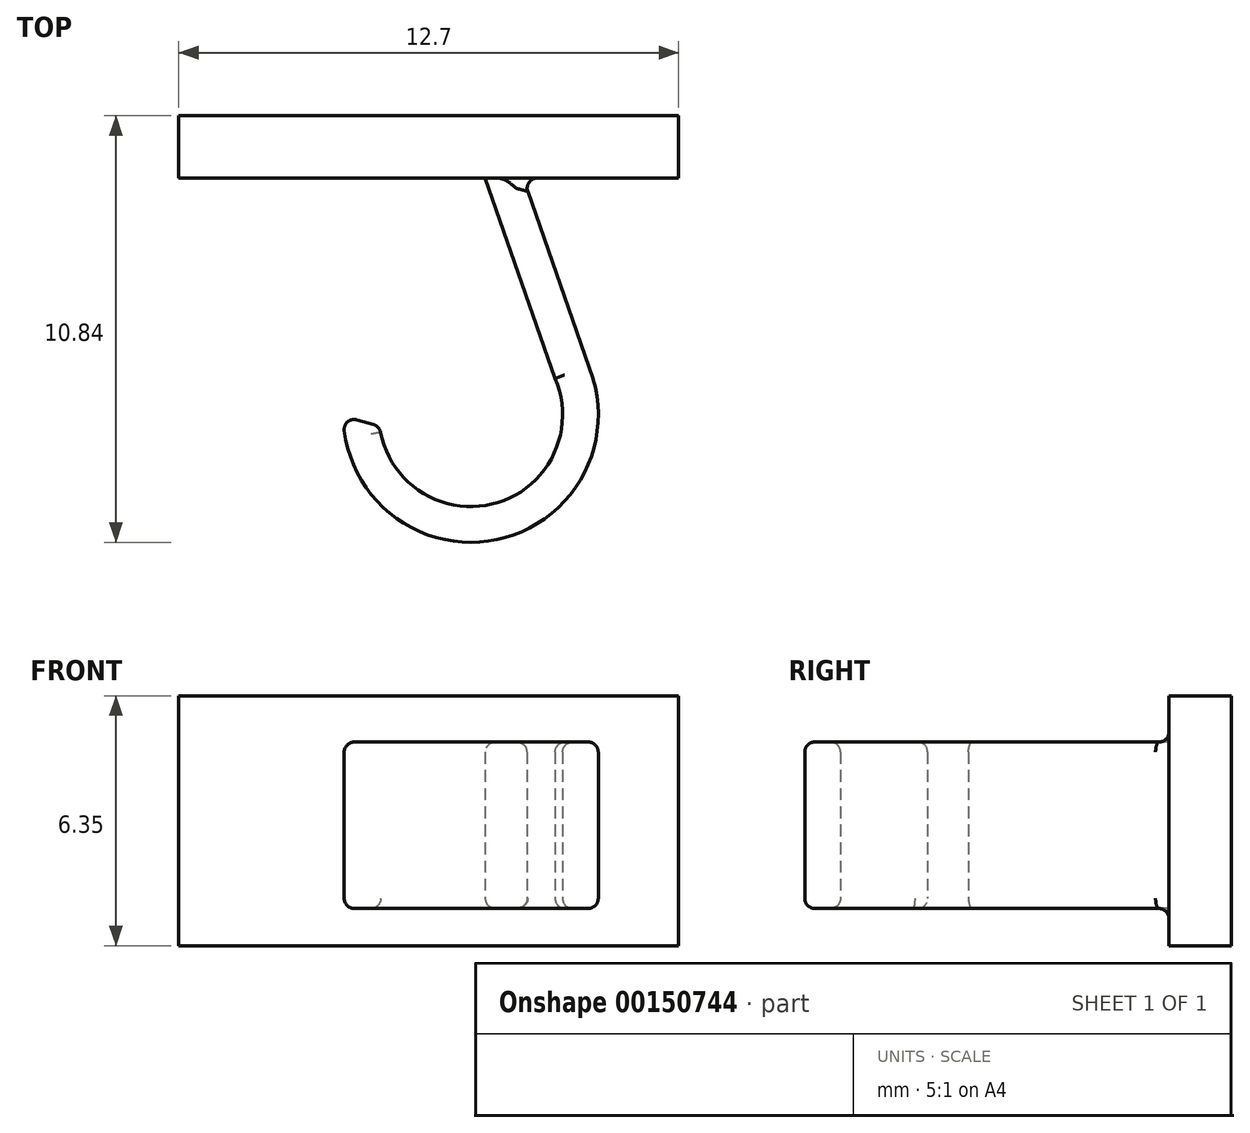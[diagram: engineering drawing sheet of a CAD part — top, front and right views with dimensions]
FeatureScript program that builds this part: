
annotation { "Feature Type Name" : "Feature", "Feature Type Description" : "" }
export const myFeature = defineFeature(function(context is Context, id is Id, definition is map)
    precondition{}
    {
        {
            var Q0;
            Q0=qCreatedBy(makeId("Front.planeOp"),FACE);
            var sketch = newSketch(context, id + "F0", { "sketchPlane" : qUnion([Q0])});
            skLineSegment(sketch, "E0.bottom", {"start": v(0, 0) * mm, "end": v(12.7, 0) * mm});
            skLineSegment(sketch, "E0.top", {"start": v(0, 6.35) * mm, "end": v(12.7, 6.35) * mm});
            skLineSegment(sketch, "E0.left", {"start": v(0, 0) * mm, "end": v(0, 6.35) * mm});
            skLineSegment(sketch, "E0.right", {"start": v(12.7, 0) * mm, "end": v(12.7, 6.35) * mm});
            skSolve(sketch);
        }
        {
            var Q0;
            Q0=makeQuery(id+"F0.imprint","IMPRINT",FACE,{"disambiguationData":[TD([[makeQuery(id+"F0.imprint","IMPRINT",EDGE,{"derivedFrom":sQuery(id+"F0.wireOp",EDGE,"E0.bottom")}),1.0]])]});
            extrude(context, id + "F1", {"entities" : qUnion([Q0]), "depth" : 1.59 * mm});
        }
        {
            var Q0;
            Q0=makeQuery(id+"F1.opExtrude","CAP_FACE",FACE,{"disambiguationData":[OSD([sQuery(id+"F0.wireOp",EDGE,"E0.bottom"),sQuery(id+"F0.wireOp",EDGE,"E0.top"),sQuery(id+"F0.wireOp",EDGE,"E0.left"),sQuery(id+"F0.wireOp",EDGE,"E0.right")])],"isStart":false});
            var sketch = newSketch(context, id + "F2", { "sketchPlane" : qUnion([Q0])});
            skLineSegment(sketch, "E1.bottom", {"start": v(7.78, 5.18) * mm, "end": v(8.75, 5.18) * mm});
            skLineSegment(sketch, "E1.top", {"start": v(7.78, 0.95) * mm, "end": v(8.75, 0.95) * mm});
            skLineSegment(sketch, "E1.left", {"start": v(7.78, 5.18) * mm, "end": v(7.78, 0.95) * mm});
            skLineSegment(sketch, "E1.right", {"start": v(8.75, 5.18) * mm, "end": v(8.75, 0.95) * mm});
            skSolve(sketch);
        }
        {
            var Q0;
            Q0=makeQuery(id+"F1.opExtrude","SWEPT_FACE",FACE,{"disambiguationData":[OSD([sQuery(id+"F0.wireOp",EDGE,"E0.bottom")])]});
            var sketch = newSketch(context, id + "F3", { "sketchPlane" : qUnion([Q0])});
            skLineSegment(sketch, "E2", {"start": v(8.29, 1.59) * mm, "end": v(10.06, 6.68) * mm});
            skArc(sketch, "E3", {"start": v(10.06, 6.68) * mm, "mid": v(7.96, 10.35) * mm, "end": v(4.62, 7.75) * mm});
            skPoint(sketch, "E4", {"position": v(4.62, 7.75) * mm});
            skSolve(sketch);
        }
        {
            var Q0;
            Q0=makeQuery(id+"F2.imprint","IMPRINT",FACE,{"disambiguationData":[TD([[makeQuery(id+"F2.imprint","IMPRINT",EDGE,{"derivedFrom":sQuery(id+"F2.wireOp",EDGE,"E1.bottom")}),-1.0]])]});
            var Q1;
            Q1=sQuery(id+"F3.wireOp",EDGE,"E2");
            var Q2;
            Q2=sQuery(id+"F3.wireOp",EDGE,"E3");
            sweep(context, id + "F4", {"operationType" : NewBodyOperationType.ADD, "profiles" : qUnion([Q0]), "path" : qUnion([Q1, Q2])});
        }
        {
            var Q0;
            Q0=makeQuery(id+"F4.opSweep","CAP_EDGE",EDGE,{"disambiguationData":[OSD([sQuery(id+"F2.wireOp",EDGE,"E1.right"),sQuery(id+"F3.wireOp",VERTEX,"E3.end")])],"isStart":false});
            var Q1;
            Q1=makeQuery(id+"F4.opSweep","CAP_EDGE",EDGE,{"disambiguationData":[OSD([sQuery(id+"F2.wireOp",EDGE,"E1.left"),sQuery(id+"F3.wireOp",VERTEX,"E3.end")])],"isStart":false});
            var Q2;
            Q2=makeQuery(id+"F4.opSweep","SWEPT_EDGE",EDGE,{"disambiguationData":[OSD([sQuery(id+"F2.wireOp",EDGE,"E1.top"),sQuery(id+"F2.wireOp",EDGE,"E1.left"),sQuery(id+"F3.wireOp",EDGE,"E3")])]});
            var Q3;
            Q3=makeQuery(id+"F4.opSweep","SWEPT_EDGE",EDGE,{"disambiguationData":[OSD([sQuery(id+"F2.wireOp",EDGE,"E1.top"),sQuery(id+"F2.wireOp",EDGE,"E1.left"),sQuery(id+"F3.wireOp",EDGE,"E2")])]});
            var Q4;
            Q4=makeQuery(id+"F4.opSweep","SWEPT_FACE",FACE,{"disambiguationData":[OSD([sQuery(id+"F2.wireOp",EDGE,"E1.right"),sQuery(id+"F3.wireOp",EDGE,"E2")])]});
            var Q5;
            Q5=makeQuery(id+"F4.opSweep","SWEPT_EDGE",EDGE,{"disambiguationData":[OSD([sQuery(id+"F2.wireOp",EDGE,"E1.top"),sQuery(id+"F2.wireOp",EDGE,"E1.right"),sQuery(id+"F3.wireOp",EDGE,"E2")])]});
            var Q6;
            Q6=makeQuery(id+"F4.opSweep","SWEPT_EDGE",EDGE,{"disambiguationData":[OSD([sQuery(id+"F2.wireOp",EDGE,"E1.top"),sQuery(id+"F2.wireOp",EDGE,"E1.right"),sQuery(id+"F3.wireOp",EDGE,"E3")])]});
            var Q7;
            Q7=makeQuery(id+"F4.opSweep","CAP_EDGE",EDGE,{"disambiguationData":[OSD([sQuery(id+"F2.wireOp",EDGE,"E1.top"),sQuery(id+"F3.wireOp",VERTEX,"E3.end")])],"isStart":false});
            var Q8;
            Q8=makeQuery(id+"F4.opSweep","CAP_EDGE",EDGE,{"disambiguationData":[OSD([sQuery(id+"F2.wireOp",EDGE,"E1.bottom"),sQuery(id+"F3.wireOp",VERTEX,"E3.end")])],"isStart":false});
            var Q9;
            Q9=makeQuery(id+"F4.opSweep","SWEPT_EDGE",EDGE,{"disambiguationData":[OSD([sQuery(id+"F2.wireOp",EDGE,"E1.bottom"),sQuery(id+"F2.wireOp",EDGE,"E1.left"),sQuery(id+"F3.wireOp",EDGE,"E3")])]});
            var Q10;
            Q10=makeQuery(id+"F4.opSweep","SWEPT_EDGE",EDGE,{"disambiguationData":[OSD([sQuery(id+"F2.wireOp",EDGE,"E1.bottom"),sQuery(id+"F2.wireOp",EDGE,"E1.left"),sQuery(id+"F3.wireOp",EDGE,"E2")])]});
            var Q11;
            Q11=makeQuery(id+"F4.opSweep","SWEPT_EDGE",EDGE,{"disambiguationData":[OSD([sQuery(id+"F2.wireOp",EDGE,"E1.bottom"),sQuery(id+"F2.wireOp",EDGE,"E1.right"),sQuery(id+"F3.wireOp",EDGE,"E3")])]});
            fillet(context, id + "F5", {"entities" : qUnion([Q0, Q1, Q2, Q3, Q4, Q5, Q6, Q7, Q8, Q9, Q10, Q11]), "radius" : 0.25 * mm, "tangentPropagation" : true, "allowEdgeOverflow" : false});
        }
    });
